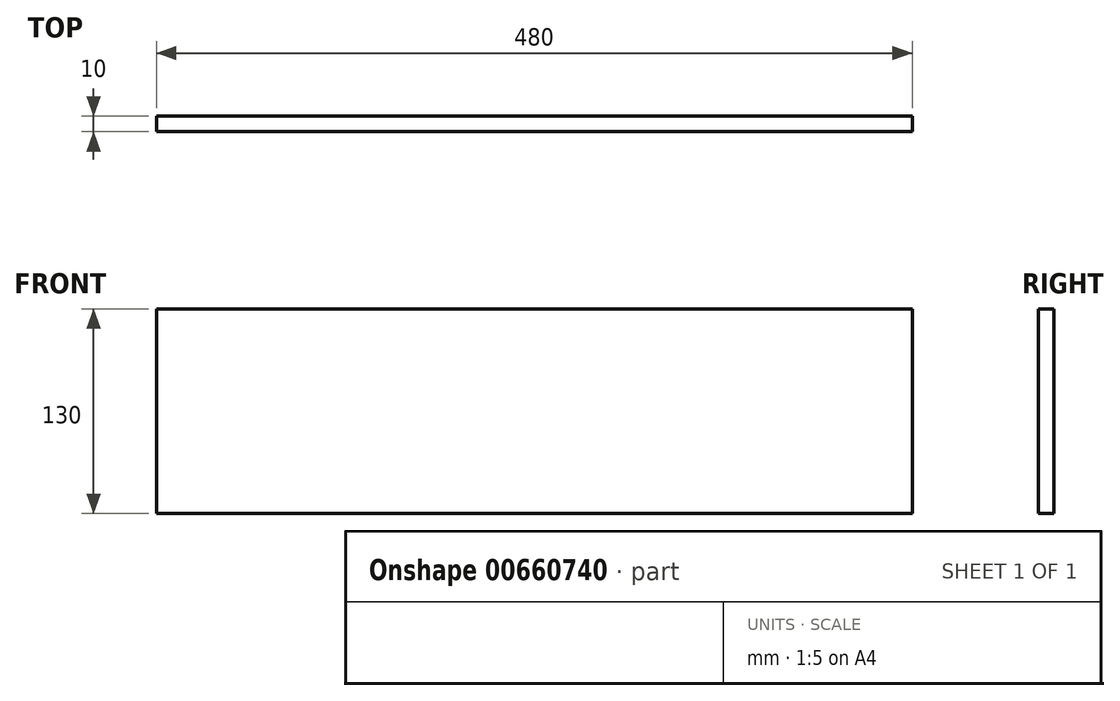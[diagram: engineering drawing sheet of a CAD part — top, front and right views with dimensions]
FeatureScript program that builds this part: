
annotation { "Feature Type Name" : "Feature", "Feature Type Description" : "" }
export const myFeature = defineFeature(function(context is Context, id is Id, definition is map)
    precondition{}
    {
        {
            var Q0;
            Q0=qCreatedBy(makeId("Front.planeOp"),FACE);
            var sketch = newSketch(context, id + "F0", { "sketchPlane" : qUnion([Q0])});
            skLineSegment(sketch, "E0.bottom", {"start": v(0, 0) * mm, "end": v(480, 0) * mm});
            skLineSegment(sketch, "E0.top", {"start": v(0, 130) * mm, "end": v(480, 130) * mm});
            skLineSegment(sketch, "E0.left", {"start": v(0, 0) * mm, "end": v(0, 130) * mm});
            skLineSegment(sketch, "E0.right", {"start": v(480, 0) * mm, "end": v(480, 130) * mm});
            skSolve(sketch);
        }
        {
            var Q0;
            Q0=makeQuery(id+"F0.imprint","IMPRINT",FACE,{"disambiguationData":[TD([[makeQuery(id+"F0.imprint","IMPRINT",EDGE,{"derivedFrom":sQuery(id+"F0.wireOp",EDGE,"E0.bottom")}),1.0]])]});
            extrude(context, id + "F1", {"entities" : qUnion([Q0]), "depth" : 10 * mm, "offsetDistance" : 25 * mm});
        }
    });
